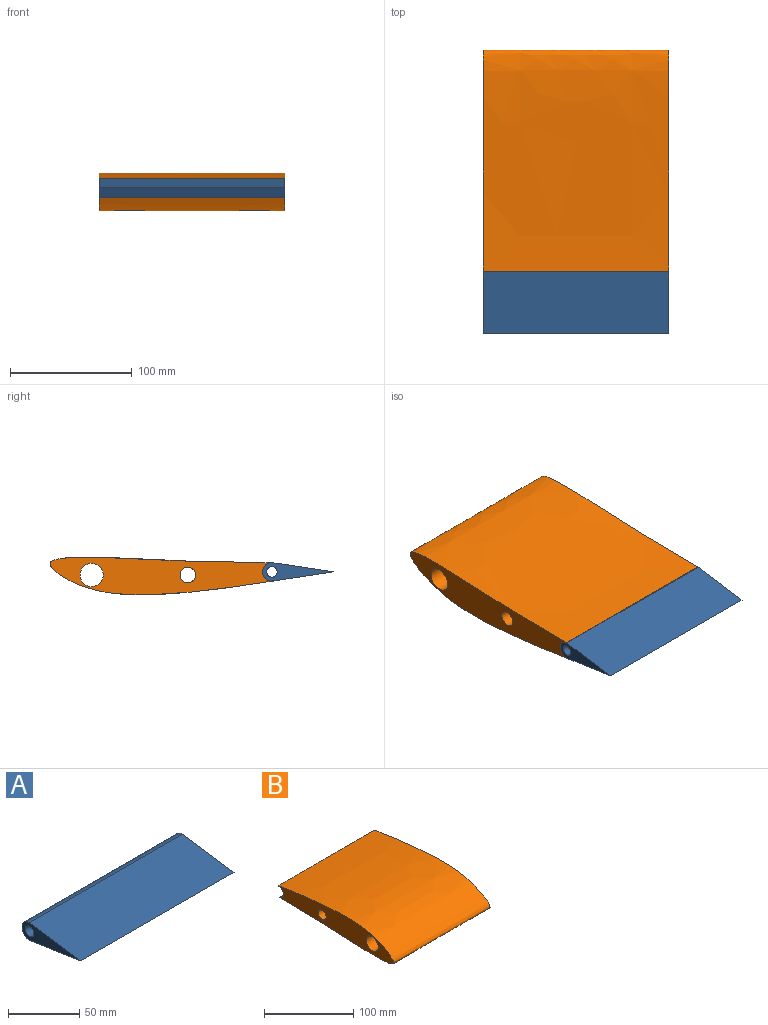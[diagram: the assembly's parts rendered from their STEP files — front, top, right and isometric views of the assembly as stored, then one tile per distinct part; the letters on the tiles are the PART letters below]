
ASSEMBLY  parts=2 mates=1
PART A: 6 faces, bbox 152.4x58.4x15.2 mm
  f0: plane 152.4x50.8mm, normal (0,-0.15,-0.99), area 7828.5mm2, adj f1,f3,f4,f5
  f1: cylinder r=7.62mm len=152.4mm, axis (1,0,0), area 3648.3mm2, adj f0,f3,f4,f5
  f2: cylinder r=4.28mm len=152.4mm, axis (1,0,0), area 4098.6mm2, adj f4,f5
  f3: plane 152.4x50.8mm, normal (0,-0.15,0.99), area 7828.5mm2, adj f0,f1,f4,f5
  f4: plane 58.42x15.24mm, normal (-1,0,0), area 420.7mm2, adj f0,f1,f2,f3
  f5: plane 58.42x15.24mm, normal (1,0,0), area 420.7mm2, adj f0,f1,f2,f3
PART B: 6 faces, bbox 152.4x198x46.2 mm
  f0: cylinder r=7.62mm len=152.4mm, axis (-1,0,0), area 3673.4mm2, adj f3,f4,f5
  f1: cylinder r=9.53mm len=152.4mm, axis (-1,0,0), area 9120.7mm2, adj f4,f5
  f2: cylinder r=6.35mm len=152.4mm, axis (-1,0,0), area 6080.5mm2, adj f4,f5
  f3: extruded ~182.88x152.4mm, area 57107.9mm2, adj f0,f4,f5
  f4: plane 197.96x46.15mm, normal (1,0,0), area 3770.8mm2, adj f0,f1,f2,f3
  f5: plane 197.96x46.15mm, normal (-1,0,0), area 3770.8mm2, adj f0,f1,f2,f3
PLACE A t=(12.09,62.65,96.35)mm
PLACE B rot(axis=(1,0,0),180deg) t=(12.09,91.93,103.94)mm
MATE fastened B.f0 <-> A.f1  axis (-1,0,0) through (12.09,62.65,96.35)mm
